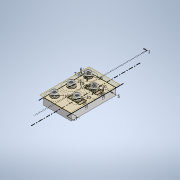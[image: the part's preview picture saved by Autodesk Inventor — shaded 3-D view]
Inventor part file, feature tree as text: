
AUTODESK INVENTOR PART (.ipt)
format: ipt  version: 2022.2 (Build 262287000, 287)  size: 5,219,328 bytes
history: native  units: mm
features: sketch x17, extrude x9, thread x5, revolve x5, helix x5, projected_geometry x4, other x3, plane x2, chamfer x1, fillet x1, reference x1
ambient origin geometry x8: Origin, YZ Plane, XZ Plane, XY Plane, X Axis, Y Axis, Z Axis, Center Point
bodies: Solid1 (feature_tree), Solid7 (feature_tree), Solid8 (feature_tree), Solid9 (feature_tree), Solid10 (feature_tree), Solid11 (feature_tree)
feature tree (53):
  sketch  "Sketch1"  dims[d0=20.0mm d1=7.92mm]
  extrude  "Base Plate"  Depth=7.92mm
  extrude  "Bearing Washer"  Depth=10.0mm
  extrude  "Straightening Pins"  Depth=1.0mm
  extrude  "Base Rails"  Depth=4.0mm
  extrude  "Slider Rails"  Depth=6.0mm
  extrude  "Nut Cavities"  Depth=10.0mm
  extrude  "Tightening Holes"  Depth=10.0mm
  extrude  "Spring Mount"  Depth=10.0mm
  chamfer  "Chamfer1"  Distance=10.0mm
  thread  "Thread1"  [1 undecoded]
  thread  "Thread2"  [1 undecoded]
  thread  "Thread3"  [1 undecoded]
  thread  "Thread4"  [1 undecoded]
  thread  "Thread5"  [1 undecoded]
  revolve  "Revolution6"  [1 undecoded]
  helix  "Coil6"  [1 undecoded]
  revolve  "Revolution7"  [1 undecoded]
  helix  "Coil7"  [1 undecoded]
  revolve  "Revolution8"  [1 undecoded]
  helix  "Coil8"  [1 undecoded]
  revolve  "Revolution9"  [1 undecoded]
  helix  "Coil9"  [1 undecoded]
  revolve  "Revolution10"  [1 undecoded]
  helix  "Coil10"  [1 undecoded]
  plane  "Work Plane3"
  sketch  "Sketch29"  dims[d188=0.7007mm d189=16.4mm d190=10.0mm d191=0.0mm d192=0.0mm d193=0.0mm d194=0.0mm d195=0.0mm d196=9.599311mm d197=0.112058mm d198=0.112058mm d201=0.7mm d203=9.599311mm d205=0.0mm d206=0.7007mm d207=16.4mm d208=10.0mm d209=0.0mm d210=0.0mm d211=0.0mm d212=0.0mm d213=0.0mm d214=9.599311mm d215=0.112058mm d216=0.112058mm d219=0.7mm d221=9.599311mm d223=0.0mm d224=0.7007mm d225=16.4mm d226=10.0mm d227=0.0mm d228=0.0mm d229=0.0mm d230=0.0mm d231=0.0mm d232=9.599311mm d233=0.112058mm d234=0.112058mm d237=0.7mm d239=9.599311mm d241=0.0mm d242=0.7007mm d243=16.4mm d244=10.0mm d245=0.0mm d246=0.0mm d247=0.0mm d248=0.0mm d249=0.0mm d250=9.599311mm d251=0.112058mm d252=0.112058mm d255=0.7mm d257=9.599311mm d259=0.0mm d260=0.7007mm d261=16.4mm d262=10.0mm d263=0.0mm d264=0.0mm d265=0.0mm d266=0.0mm d267=0.0mm d268=0.0mm d269=0.0mm d272=2.0mm d273=4.0mm d274=2.0mm]
  plane  "Work Plane4"
  extrude  "Extrusion13"  Depth=9.599311mm
  fillet  "Fillet1"  [1 undecoded]
  sketch  "Sketch2"  dims[d2=4.2mm d3=30.0mm d5=25.0mm d6=10.0mm d8=10.0mm]
  projected_geometry  "Projected Loop1"
  projected_geometry  "Projected Loop2"
  projected_geometry  "Projected Loop3"
  projected_geometry  "Projected Loop4"
  sketch  "Sketch3"  dims[d10=20.0mm d11=7.92mm d12=4.2mm d13=1.0mm]
  sketch  "Sketch4"  dims[d14=4.0mm d15=4.0mm]
  sketch  "Sketch5"  dims[d16=6.0mm d17=6.0mm]
  sketch  "Sketch6"  dims[d19=5.0mm d20=10.0mm]
  sketch  "Sketch19"  dims[d33=10.0mm d34=10.0mm]
  sketch  "Sketch20"  dims[d35=10.0mm d36=10.0mm]
  sketch  "Sketch21"  dims[d37=10.0mm d38=10.0mm d39=0.0mm d40=1.0mm d41=0.0mm d42=6.0mm d43=0.0mm d44=135.0deg d45=135.0deg d46=0.4mm]
  sketch  "Sketch22"  dims[d47=5.0mm d48=0.0mm d49=10.0mm d50=0.0mm d51=7.1mm]
  sketch  "Sketch23"  dims[d52=3.0mm d53=0.0mm d54=4.2mm d55=3.0mm d56=0.0mm]
  sketch  "Sketch24"  dims[d57=6.0mm d58=6.0mm d59=2.0mm d60=0.0mm d61=0.0mm]
  sketch  "Sketch25"  dims[d68=15.0mm d69=0.0mm d70=15.0mm d71=0.0mm d72=15.0mm d73=0.0mm d74=15.0mm d75=0.0mm d76=15.0mm d77=0.0mm d78=1.0mm d79=2.0mm d80=45.0deg d88=9.599311mm]
  sketch  "Sketch26"  dims[d106=9.599311mm d124=9.599311mm d142=9.599311mm]
  sketch  "Sketch27"  dims[d160=9.599311mm d171=7.0mm d178=9.599311mm d179=0.112058mm d180=0.112058mm]
  sketch  "Sketch28"  dims[d183=0.7mm d185=9.599311mm d187=0.0mm]
  reference  "Reference1"
  other  "<userpath>\Documents\Inventor\Wire Bender\Assembly.iam"
  other  "Assembly.iam"
  other  "Feed Motor Mount:1"
note: 16 required parameter values undecoded (feature->parameter linkage not recoverable at this tier; creation-order binding heuristic only, values carry confidence <= 0.55)